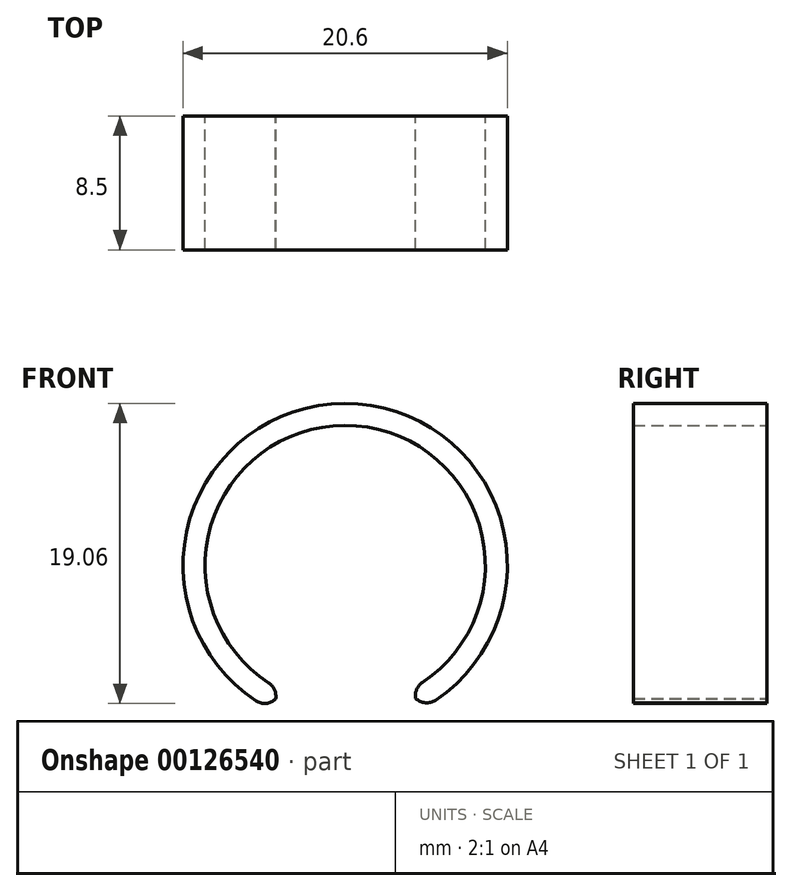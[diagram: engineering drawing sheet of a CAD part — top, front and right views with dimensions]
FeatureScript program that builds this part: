
annotation { "Feature Type Name" : "Feature", "Feature Type Description" : "" }
export const myFeature = defineFeature(function(context is Context, id is Id, definition is map)
    precondition{}
    {
        {
            var Q0;
            Q0=qCreatedBy(makeId("Front.planeOp"),FACE);
            var sketch = newSketch(context, id + "F0", { "sketchPlane" : qUnion([Q0])});
            skArc(sketch, "E0", {"start": v(4.14, -7.88) * mm, "mid": v(-0.03, 8.9) * mm, "end": v(-4.08, -7.91) * mm});
            skArc(sketch, "E1", {"start": v(4.79, -9.12) * mm, "mid": v(-0.04, 10.3) * mm, "end": v(-4.72, -9.16) * mm});
            skLineSegment(sketch, "E2", {"start": v(-4.08, -7.91) * mm, "end": v(-4.72, -9.16) * mm});
            skLineSegment(sketch, "E3", {"start": v(4.14, -7.88) * mm, "end": v(4.79, -9.12) * mm});
            skSolve(sketch);
        }
        {
            var Q0;
            Q0=makeQuery(id+"F0.imprint","IMPRINT",FACE,{"disambiguationData":[TD([[makeQuery(id+"F0.imprint","IMPRINT",EDGE,{"derivedFrom":sQuery(id+"F0.wireOp",EDGE,"E0")}),-1.0]])]});
            extrude(context, id + "F1", {"entities" : qUnion([Q0]), "depth" : 8.5 * mm});
        }
        {
            var Q0;
            Q0=makeQuery(id+"F1.opExtrude","SWEPT_EDGE",EDGE,{"disambiguationData":[OSD([sQuery(id+"F0.wireOp",EDGE,"E0"),sQuery(id+"F0.wireOp",EDGE,"E2")])]});
            var Q1;
            Q1=makeQuery(id+"F1.opExtrude","SWEPT_EDGE",EDGE,{"disambiguationData":[OSD([sQuery(id+"F0.wireOp",EDGE,"E0"),sQuery(id+"F0.wireOp",EDGE,"E3")])]});
            var Q2;
            Q2=makeQuery(id+"F1.opExtrude","SWEPT_EDGE",EDGE,{"disambiguationData":[OSD([sQuery(id+"F0.wireOp",EDGE,"E1"),sQuery(id+"F0.wireOp",EDGE,"E3")])]});
            var Q3;
            Q3=makeQuery(id+"F1.opExtrude","SWEPT_EDGE",EDGE,{"disambiguationData":[OSD([sQuery(id+"F0.wireOp",EDGE,"E1"),sQuery(id+"F0.wireOp",EDGE,"E2")])]});
            fillet(context, id + "F2", {"entities" : qUnion([Q0, Q1, Q2, Q3]), "radius" : 1 * mm, "tangentPropagation" : true, "allowEdgeOverflow" : false});
        }
    });
